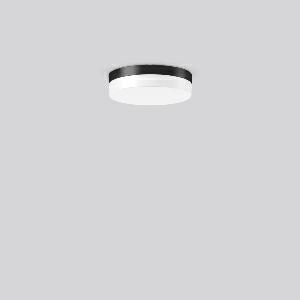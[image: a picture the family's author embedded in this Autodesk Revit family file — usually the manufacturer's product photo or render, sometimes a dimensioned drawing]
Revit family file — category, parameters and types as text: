
# Revit family: flat_slim_round_312132_0031_76_da21
name_source: partatom
category: Lighting Fixtures
units: mm (PartAtom-declared; Revit-internal decimal feet)

## family parameters
Cut with Voids When Loaded = No
Host = Face
Light Source = No
Part Type = Normal
Room Calculation Point = No
Round Connector Dimension = Use Diameter
Shared = No

## types (1)
- FLAT SLIM round (1 x LED Modul 830, 1000 lm, 3000)
    Apparent Load = 12 VA
    CIE Flux Codes = 42 72 91 89 100
    Color Rendering = 80
    Color Temperature = 3000
    Default Elevation = 1800 mm
    Height = 63 mm
    Lamp = 1 x LED Modul 830
    Lamp Light Flux = 1000 lm
    Lamp count = 1
    Length = 230 mm
    Lifetime = 50000 h
    Luminous efficacy = 83 lm/W
    Manufacturer = RZB
    ModVariant = No
    Model = 312132.0031.76
    Mounting Place = Ceiling, Wall
    Mounting Type = Surface mounted
    Number of Poles = 1
    OnlyDefault = Yes
    Power Factor = 1
    Product Name = FLAT SLIM round
    Product group = Surface mounted ceiling and wall luminaires
    ProductGroupID = 305
    Protection Class = Protection class I
    Protection Degree = IP 65
    RLX_Detail_Level = 1
    RLX_Emergency_Light_Flux = 0 lm
    RLX_Emergency_Type = 0
    RLX_Emergency_Type_DB = No
    RlxData = <blob elided: 17865 chars, md5=a959bb81>
    Socket = socket
    Standby Power = 0 W
    System Light Flux = 1000 lm
    System Power = 12 W
    Type Comments = Product without accessories
    Type Image = 312132.0031.jpg
    URL = http://relux.com
    VarID = ---
    Voltage = 230 V
    Voltage Range = 220-240 V
    Weight = 0.00 kg
    Width = 0 mm  [stored 0 ft]

note: [stored X ft] marks values corroborated as IEEE doubles in the binary element streams (Revit-internal decimal feet)

## geometry (parser evidence)
native form markers: Blend x4, Sweep x14
no freeform markers — native parametric forms only
